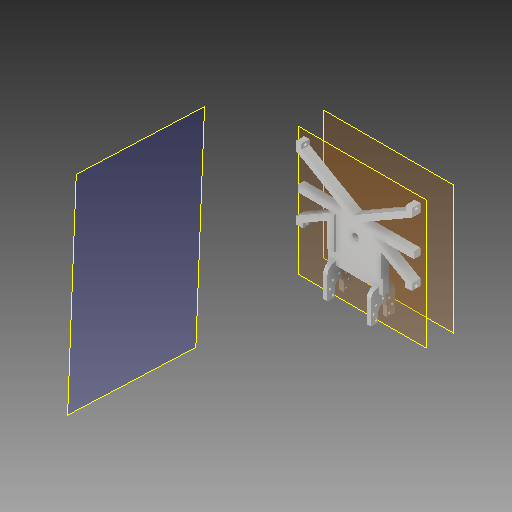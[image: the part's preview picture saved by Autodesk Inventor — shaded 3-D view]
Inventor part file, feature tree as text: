
AUTODESK INVENTOR PART (.ipt)
format: ipt  version: 2019 (Build 230136000, 136)  size: 4,199,424 bytes
history: native  units: in
note: dims shown in document units (in); Inventor stores cm internally (conversion verified against a paired STEP export)
features: sketch x4, other x3, split x2, plane x2, extrude x2
ambient origin geometry x8: Origin, YZ Plane, XZ Plane, XY Plane, X Axis, Y Axis, Z Axis, Center Point
bodies: Solid1 (feature_tree)
feature tree (13):
  other  "1812NicoHead1.ipt"
  split  "Split4"
  split  "Split5"
  plane  "Work Plane2"
  extrude  "Extrusion1"  Depth=0.0394in
  plane  "Work Plane3"
  extrude  "Extrusion2"  Depth=0.3937in TaperAngle=0.0deg
  other  "Solid2::1812NicoHead1.ipt"
  other  "TaggingFeature1"
  sketch  "Sketch5"  dims[d0=0.3937in d3=0.0394in]
  sketch  "Sketch6"  dims[d4=0.0197in d5=0.3937in d6=0.0in]
  sketch  "Sketch7"  dims[d7=-1.25in]
  sketch  "Sketch8"  dims[d8=0.3937in d9=0.0in]
